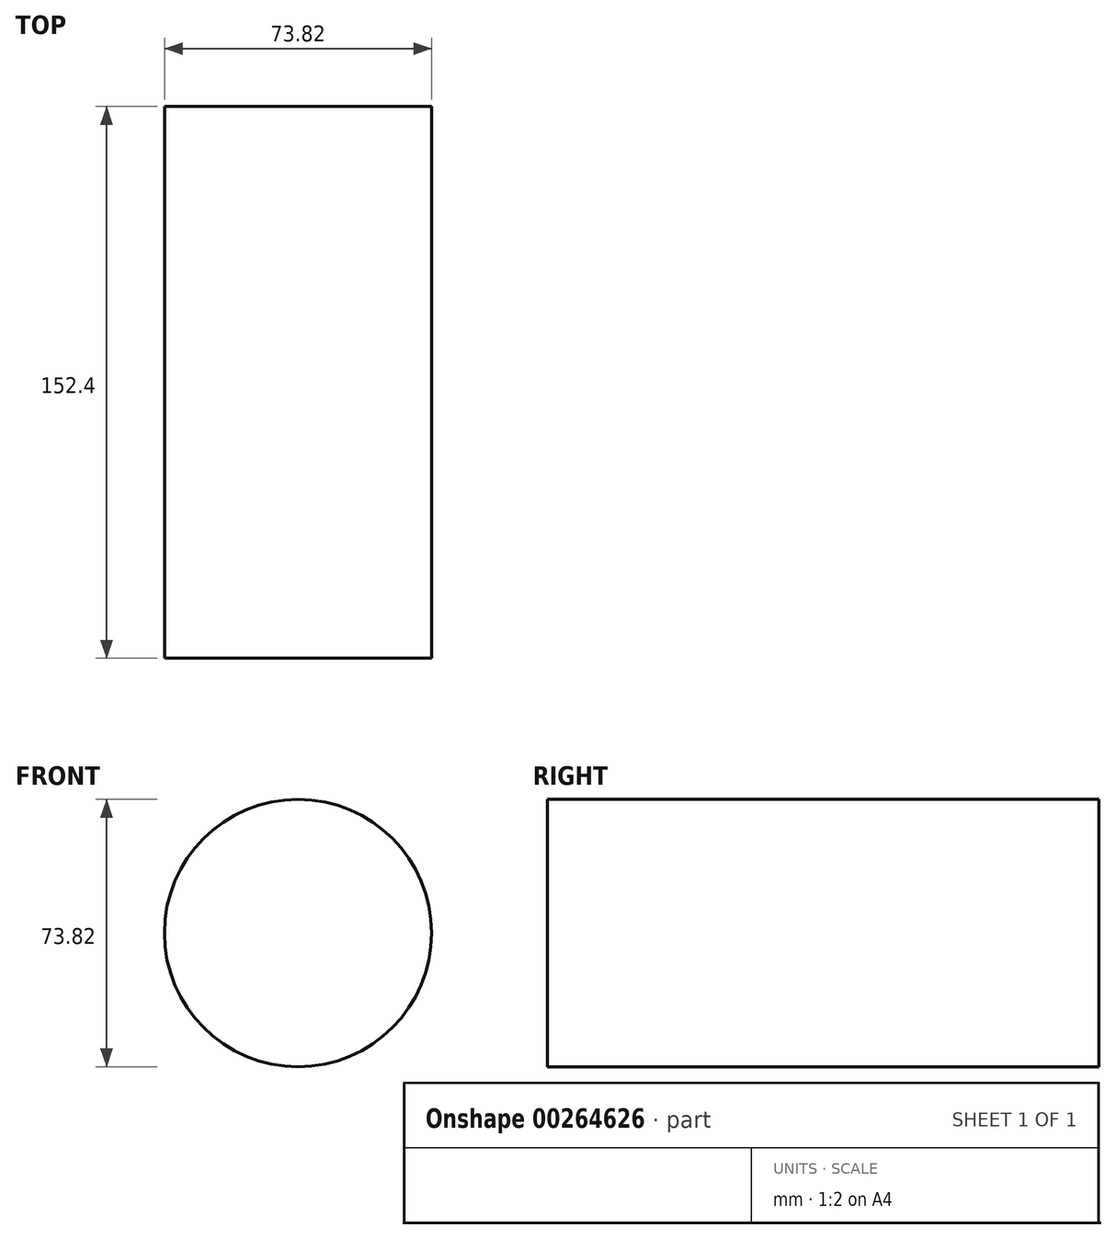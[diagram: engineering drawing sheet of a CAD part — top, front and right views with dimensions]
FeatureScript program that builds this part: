
annotation { "Feature Type Name" : "Feature", "Feature Type Description" : "" }
export const myFeature = defineFeature(function(context is Context, id is Id, definition is map)
    precondition{}
    {
        {
            var Q0;
            Q0=qCreatedBy(makeId("Front.planeOp"),FACE);
            var sketch = newSketch(context, id + "F0", { "sketchPlane" : qUnion([Q0])});
            skCircle(sketch, "E0", {"center": v(0, 0) * mm, "radius": 36.91 * mm});
            skSolve(sketch);
        }
        {
            var Q0;
            Q0=makeQuery(id+"F0.imprint","IMPRINT",FACE,{"disambiguationData":[TD([[makeQuery(id+"F0.imprint","IMPRINT",EDGE,{"derivedFrom":sQuery(id+"F0.wireOp",EDGE,"E0")}),1.0]])]});
            extrude(context, id + "F1", {"entities" : qUnion([Q0]), "depth" : 152.4 * mm, "symmetric" : true});
        }
    });
